# Revit family: QF_BOURGEAT_HARMONIE_table_pre_tri_modèles_hauteur_standard
name_source: partatom
category: Equipement spécialisé
revit_build: Autodesk Revit 2015 (Build: 20140606_1530(x64)
units: mm (PartAtom-declared; Revit-internal decimal feet)

## types (6) — shared parameters
Fabricant = BOURGEAT
Hauteur hors tout = 1157 mm  [stored 3.79593 ft]
Hauteur plan de travail = 830 mm  [stored 2.7231 ft]
Inox = Acier inoxydable, poli
Profondeur hors tout = 761 mm  [stored 2.49672 ft]
Spécification du Fabricant = Table de tri harmonie
URL catalogue = http://www.bourgeat.fr
Vert = Vert

## per-type parameters (varying)
| type | Décalage du sol | Hauteur porte | Longueur hors tout | Modèle | Panneau arrière | Panneau avant | Pieds | Poids net à vide | Portes arrière | Portes avant | Roulettes | montant_arriere | montant_avant | pied_arriere | pied_avant | roue_arriere | roue_avant |
| Modèle sur pieds - sans portes | 27 mm  [stored 0.0885827 ft] | 713 mm | 2016 mm  [stored 6.61417 ft] | 8582602 | Oui | Non | Oui | 95.00 kg | Non | Non | Non | Non | Oui | Non | Oui | Non | Non |
| Modèle sur pieds - portes arrière | 27 mm  [stored 0.0885827 ft] | 713 mm | 2016 mm  [stored 6.61417 ft] | 858261 | Non | Oui | Oui | 105.00 kg | Oui | Non | Non | Oui | Non | Oui | Non | Non | Non |
| Modèle sur pieds - portes avant | 27 mm  [stored 0.0885827 ft] | 713 mm | 2016 mm  [stored 6.61417 ft] | 858262 | Oui | Non | Oui | 105.00 kg | Non | Oui | Non | Non | Oui | Non | Oui | Non | Non |
| Modèle sur roues - sans portes | 184 mm  [stored 0.603675 ft] | 553 mm  [stored 1.8143 ft] | 2036 mm  [stored 6.67979 ft] | 858330 | Oui | Non | Non | 81.00 kg | Non | Non | Oui | Non | Oui | Non | Non | Non | Oui |
| Modèle sur roues - portes arrière | 184 mm  [stored 0.603675 ft] | 553 mm  [stored 1.8143 ft] | 2036 mm  [stored 6.67979 ft] | 858331 | Non | Oui | Non | 105.00 kg | Oui | Non | Oui | Oui | Non | Non | Non | Oui | Non |
| Modèle sur roues - portes avant | 184 mm  [stored 0.603675 ft] | 553 mm  [stored 1.8143 ft] | 2036 mm  [stored 6.67979 ft] | 858332 | Oui | Non | Non | 81.00 kg | Non | Oui | Oui | Non | Oui | Non | Non | Non | Oui |

note: [stored X ft] marks values corroborated as IEEE doubles in the binary element streams (Revit-internal decimal feet)

## geometry (parser evidence)
native form markers: Blend x8
no freeform markers — native parametric forms only
